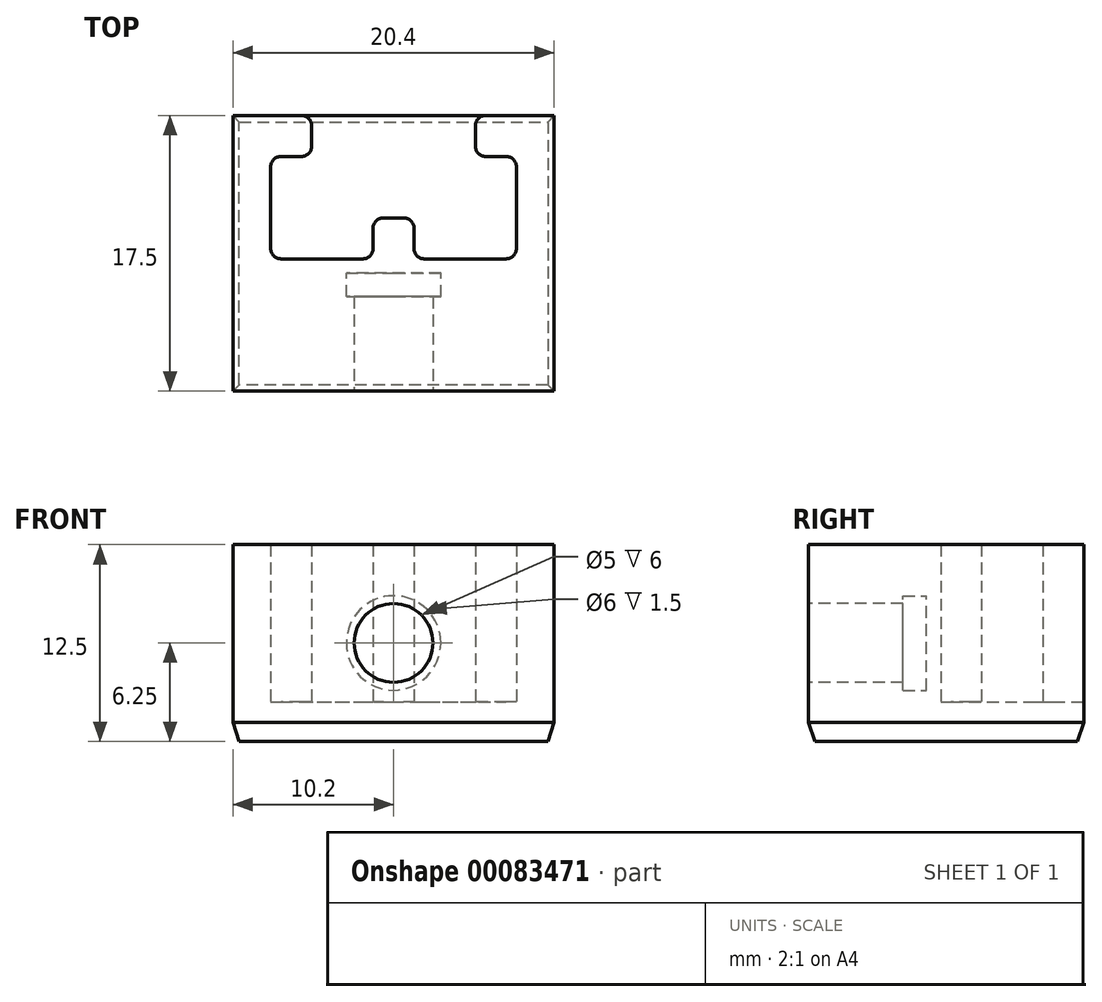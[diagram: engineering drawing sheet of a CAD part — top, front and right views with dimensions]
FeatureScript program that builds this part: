
annotation { "Feature Type Name" : "Feature", "Feature Type Description" : "" }
export const myFeature = defineFeature(function(context is Context, id is Id, definition is map)
    precondition{}
    {
        {
            var Q0;
            Q0=qCreatedBy(makeId("Top.planeOp"),FACE);
            var sketch = newSketch(context, id + "F0", { "sketchPlane" : qUnion([Q0])});
            skLineSegment(sketch, "E0", {"start": v(0, 0) * mm, "end": v(0, 11.5) * mm});
            skLineSegment(sketch, "E1", {"start": v(0, 11.5) * mm, "end": v(5, 11.5) * mm});
            skLineSegment(sketch, "E2", {"start": v(5, 11.5) * mm, "end": v(5, 8.9) * mm});
            skLineSegment(sketch, "E3", {"start": v(5, 8.9) * mm, "end": v(2.4, 8.9) * mm});
            skLineSegment(sketch, "E4", {"start": v(2.4, 8.9) * mm, "end": v(2.4, 2.4) * mm});
            skLineSegment(sketch, "E5", {"start": v(2.4, 2.4) * mm, "end": v(8.9, 2.4) * mm});
            skLineSegment(sketch, "E6", {"start": v(8.9, 2.4) * mm, "end": v(8.9, 5) * mm});
            skLineSegment(sketch, "E7", {"start": v(8.9, 5) * mm, "end": v(11.5, 5) * mm});
            skLineSegment(sketch, "E8", {"start": v(11.5, 5) * mm, "end": v(11.5, 2.4) * mm});
            skLineSegment(sketch, "E9", {"start": v(11.5, 2.4) * mm, "end": v(18, 2.4) * mm});
            skLineSegment(sketch, "E10", {"start": v(18, 2.4) * mm, "end": v(18, 8.9) * mm});
            skLineSegment(sketch, "E11", {"start": v(18, 8.9) * mm, "end": v(15.4, 8.9) * mm});
            skLineSegment(sketch, "E12", {"start": v(15.4, 8.9) * mm, "end": v(15.4, 11.5) * mm});
            skLineSegment(sketch, "E13", {"start": v(15.4, 11.5) * mm, "end": v(20.4, 11.5) * mm});
            skLineSegment(sketch, "E14", {"start": v(20.4, 11.5) * mm, "end": v(20.4, 0) * mm});
            skLineSegment(sketch, "E15", {"start": v(20.4, 0) * mm, "end": v(0, 0) * mm});
            skLineSegment(sketch, "E16", {"start": v(2.4, 2.4) * mm, "end": v(0, 2.4) * mm, "construction": true});
            skLineSegment(sketch, "E17", {"start": v(2.4, 2.4) * mm, "end": v(2.4, 0) * mm, "construction": true});
            skSolve(sketch);
        }
        {
            var Q0;
            Q0=makeQuery(id+"F0.imprint","IMPRINT",FACE,{"disambiguationData":[TD([[makeQuery(id+"F0.imprint","IMPRINT",EDGE,{"derivedFrom":sQuery(id+"F0.wireOp",EDGE,"E0")}),-1.0]])]});
            extrude(context, id + "F1", {"entities" : qUnion([Q0]), "depth" : 10 * mm, "offsetDistance" : 25 * mm});
        }
        {
            var Q0;
            Q0=makeQuery(id+"F1.opExtrude","SWEPT_EDGE",EDGE,{"disambiguationData":[OSD([sQuery(id+"F0.wireOp",EDGE,"E3"),sQuery(id+"F0.wireOp",EDGE,"E4")])]});
            var Q1;
            Q1=makeQuery(id+"F1.opExtrude","SWEPT_EDGE",EDGE,{"disambiguationData":[OSD([sQuery(id+"F0.wireOp",EDGE,"E4"),sQuery(id+"F0.wireOp",EDGE,"E5")])]});
            var Q2;
            Q2=makeQuery(id+"F1.opExtrude","SWEPT_EDGE",EDGE,{"disambiguationData":[OSD([sQuery(id+"F0.wireOp",EDGE,"E8"),sQuery(id+"F0.wireOp",EDGE,"E9")])]});
            var Q3;
            Q3=makeQuery(id+"F1.opExtrude","SWEPT_EDGE",EDGE,{"disambiguationData":[OSD([sQuery(id+"F0.wireOp",EDGE,"E5"),sQuery(id+"F0.wireOp",EDGE,"E6")])]});
            var Q4;
            Q4=makeQuery(id+"F1.opExtrude","SWEPT_EDGE",EDGE,{"disambiguationData":[OSD([sQuery(id+"F0.wireOp",EDGE,"E9"),sQuery(id+"F0.wireOp",EDGE,"E10")])]});
            var Q5;
            Q5=makeQuery(id+"F1.opExtrude","SWEPT_EDGE",EDGE,{"disambiguationData":[OSD([sQuery(id+"F0.wireOp",EDGE,"E10"),sQuery(id+"F0.wireOp",EDGE,"E11")])]});
            var Q6;
            Q6=makeQuery(id+"F1.opExtrude","SWEPT_EDGE",EDGE,{"disambiguationData":[OSD([sQuery(id+"F0.wireOp",EDGE,"E11"),sQuery(id+"F0.wireOp",EDGE,"E12")])]});
            var Q7;
            Q7=makeQuery(id+"F1.opExtrude","SWEPT_EDGE",EDGE,{"disambiguationData":[OSD([sQuery(id+"F0.wireOp",EDGE,"E12"),sQuery(id+"F0.wireOp",EDGE,"E13")])]});
            var Q8;
            Q8=makeQuery(id+"F1.opExtrude","SWEPT_EDGE",EDGE,{"disambiguationData":[OSD([sQuery(id+"F0.wireOp",EDGE,"E2"),sQuery(id+"F0.wireOp",EDGE,"E3")])]});
            var Q9;
            Q9=makeQuery(id+"F1.opExtrude","SWEPT_EDGE",EDGE,{"disambiguationData":[OSD([sQuery(id+"F0.wireOp",EDGE,"E1"),sQuery(id+"F0.wireOp",EDGE,"E2")])]});
            var Q10;
            Q10=makeQuery(id+"F1.opExtrude","SWEPT_EDGE",EDGE,{"disambiguationData":[OSD([sQuery(id+"F0.wireOp",EDGE,"E7"),sQuery(id+"F0.wireOp",EDGE,"E8")])]});
            var Q11;
            Q11=makeQuery(id+"F1.opExtrude","SWEPT_EDGE",EDGE,{"disambiguationData":[OSD([sQuery(id+"F0.wireOp",EDGE,"E6"),sQuery(id+"F0.wireOp",EDGE,"E7")])]});
            fillet(context, id + "F2", {"entities" : qUnion([Q0, Q1, Q2, Q3, Q4, Q5, Q6, Q7, Q8, Q9, Q10, Q11]), "radius" : .65 * mm, "tangentPropagation" : true, "allowEdgeOverflow" : false});
        }
        {
            var Q0;
            Q0=makeQuery(id+"F1.opExtrude","CAP_FACE",FACE,{"disambiguationData":[OSD([sQuery(id+"F0.wireOp",EDGE,"E0"),sQuery(id+"F0.wireOp",EDGE,"E1"),sQuery(id+"F0.wireOp",EDGE,"E2"),sQuery(id+"F0.wireOp",EDGE,"E3"),sQuery(id+"F0.wireOp",EDGE,"E4"),sQuery(id+"F0.wireOp",EDGE,"E5"),sQuery(id+"F0.wireOp",EDGE,"E6"),sQuery(id+"F0.wireOp",EDGE,"E7"),sQuery(id+"F0.wireOp",EDGE,"E8"),sQuery(id+"F0.wireOp",EDGE,"E9"),sQuery(id+"F0.wireOp",EDGE,"E10"),sQuery(id+"F0.wireOp",EDGE,"E11"),sQuery(id+"F0.wireOp",EDGE,"E12"),sQuery(id+"F0.wireOp",EDGE,"E13"),sQuery(id+"F0.wireOp",EDGE,"E14"),sQuery(id+"F0.wireOp",EDGE,"E15")])],"isStart":true});
            var sketch = newSketch(context, id + "F3", { "sketchPlane" : qUnion([Q0])});
            skLineSegment(sketch, "E18.bottom", {"start": v(0, 0) * mm, "end": v(20.4, 0) * mm});
            skLineSegment(sketch, "E18.top", {"start": v(0, -11.5) * mm, "end": v(20.4, -11.5) * mm});
            skLineSegment(sketch, "E18.left", {"start": v(0, 0) * mm, "end": v(0, -11.5) * mm});
            skLineSegment(sketch, "E18.right", {"start": v(20.4, 0) * mm, "end": v(20.4, -11.5) * mm});
            skSolve(sketch);
        }
        {
            var Q0;
            {var subQ7=sQuery(id+"F0.wireOp",EDGE,"E2");Q0=makeQuery(id+"F3.imprint","IMPRINT",FACE,{"disambiguationData":[TD([[makeQuery(id+"F3.imprint","IMPRINT",EDGE,{"derivedFrom":makeQuery(id+"F1.opExtrude","CAP_EDGE",EDGE,{"disambiguationData":[OSD([subQ7])],"isStart":true})}),-1.0]])]});}
            var Q1;
            Q1=makeQuery(id+"F3.imprint","IMPRINT",FACE,{"disambiguationData":[TD([[makeQuery(id+"F3.imprint","IMPRINT",EDGE,{"derivedFrom":sQuery(id+"F3.wireOp",EDGE,"E18.bottom")}),1.0]])]});
            extrude(context, id + "F4", {"entities" : qUnion([Q0, Q1]), "operationType" : NewBodyOperationType.ADD, "depth" : 2.5 * mm, "offsetDistance" : 25 * mm});
        }
        {
            var Q0;
            Q0=qCreatedBy(makeId("Top.planeOp"),FACE);
            var sketch = newSketch(context, id + "F5", { "sketchPlane" : qUnion([Q0])});
            skPoint(sketch, "E19.0", {"position": v(20.4, 0) * mm});
            skLineSegment(sketch, "E20.bottom", {"start": v(0, 0) * mm, "end": v(20.4, 0) * mm});
            skLineSegment(sketch, "E20.top", {"start": v(0, -6) * mm, "end": v(20.4, -6) * mm});
            skLineSegment(sketch, "E20.left", {"start": v(0, 0) * mm, "end": v(0, -6) * mm});
            skLineSegment(sketch, "E20.right", {"start": v(20.4, 0) * mm, "end": v(20.4, -6) * mm});
            skSolve(sketch);
        }
        {
            var Q0;
            Q0=makeQuery(id+"F5.imprint","IMPRINT",FACE,{"disambiguationData":[TD([[makeQuery(id+"F5.imprint","IMPRINT",EDGE,{"derivedFrom":sQuery(id+"F5.wireOp",EDGE,"E20.bottom")}),-1.0]])]});
            var Q1;
            Q1=makeQuery(id+"F1.opExtrude","CAP_FACE",FACE,{"disambiguationData":[OSD([sQuery(id+"F0.wireOp",EDGE,"E0"),sQuery(id+"F0.wireOp",EDGE,"E1"),sQuery(id+"F0.wireOp",EDGE,"E2"),sQuery(id+"F0.wireOp",EDGE,"E3"),sQuery(id+"F0.wireOp",EDGE,"E4"),sQuery(id+"F0.wireOp",EDGE,"E5"),sQuery(id+"F0.wireOp",EDGE,"E6"),sQuery(id+"F0.wireOp",EDGE,"E7"),sQuery(id+"F0.wireOp",EDGE,"E8"),sQuery(id+"F0.wireOp",EDGE,"E9"),sQuery(id+"F0.wireOp",EDGE,"E10"),sQuery(id+"F0.wireOp",EDGE,"E11"),sQuery(id+"F0.wireOp",EDGE,"E12"),sQuery(id+"F0.wireOp",EDGE,"E13"),sQuery(id+"F0.wireOp",EDGE,"E14"),sQuery(id+"F0.wireOp",EDGE,"E15")])],"isStart":false});
            extrude(context, id + "F6", {"entities" : qUnion([Q0]), "operationType" : NewBodyOperationType.ADD, "endBound" : BoundingType.UP_TO_SURFACE, "depth" : 10.3 * mm, "endBoundEntityFace" : qUnion([Q1]), "offsetDistance" : 25 * mm});
        }
        {
            var Q0;
            Q0=makeQuery(id+"F6.opExtrude","CAP_FACE",FACE,{"disambiguationData":[OSD([sQuery(id+"F5.wireOp",EDGE,"E20.bottom"),sQuery(id+"F5.wireOp",EDGE,"E20.top"),sQuery(id+"F5.wireOp",EDGE,"E20.left"),sQuery(id+"F5.wireOp",EDGE,"E20.right")])],"isStart":true});
            var Q1;
            Q1=makeQuery(id+"F4.opExtrude","CAP_FACE",FACE,{"disambiguationData":[OSD([sQuery(id+"F3.wireOp",EDGE,"E18.bottom"),sQuery(id+"F3.wireOp",EDGE,"E18.top"),sQuery(id+"F3.wireOp",EDGE,"E18.left"),sQuery(id+"F3.wireOp",EDGE,"E18.right")])],"isStart":false});
            extrude(context, id + "F7", {"entities" : qUnion([Q0]), "operationType" : NewBodyOperationType.ADD, "endBound" : BoundingType.UP_TO_SURFACE, "depth" : 25 * mm, "endBoundEntityFace" : qUnion([Q1]), "offsetDistance" : 25 * mm});
        }
        {
            var Q0;
            {var subQ0=sQuery(id+"F5.wireOp",EDGE,"E20.top");Q0=makeQuery(id+"F7.boolean.opBoolean","MERGE",FACE,{"derivedFrom":[makeQuery(id+"F6.opExtrude","SWEPT_FACE",FACE,{"disambiguationData":[OSD([subQ0])]}),makeQuery(id+"F7.opExtrude","SWEPT_FACE",FACE,{"disambiguationData":[OSD([subQ0])]})]});}
            var sketch = newSketch(context, id + "F8", { "sketchPlane" : qUnion([Q0])});
            skCircle(sketch, "E21", {"center": v(10.2, 3.75) * mm, "radius": 2.5 * mm});
            skLineSegment(sketch, "E22", {"start": v(10.2, 10) * mm, "end": v(10.2, -2.5) * mm, "construction": true});
            skSolve(sketch);
        }
        {
            var Q0;
            Q0=makeQuery(id+"F8.imprint","IMPRINT",FACE,{"disambiguationData":[TD([[makeQuery(id+"F8.imprint","IMPRINT",EDGE,{"derivedFrom":sQuery(id+"F8.wireOp",EDGE,"E21")}),1.0]])]});
            extrude(context, id + "F9", {"entities" : qUnion([Q0]), "operationType" : NewBodyOperationType.REMOVE, "oppositeDirection" : true, "depth" : 7.5 * mm, "offsetDistance" : 25 * mm});
        }
        {
            var Q0;
            Q0=makeQuery(id+"F9.boolean.opBoolean","COPY",FACE,{"derivedFrom":makeQuery(id+"F9.opExtrude","CAP_FACE",FACE,{"disambiguationData":[OSD([sQuery(id+"F8.wireOp",EDGE,"E21")])],"isStart":false})});
            var sketch = newSketch(context, id + "F10", { "sketchPlane" : qUnion([Q0])});
            skCircle(sketch, "E23.0", {"center": v(10.2, 3.75) * mm, "radius": 2.5 * mm, "construction": true});
            skCircle(sketch, "E24", {"center": v(10.2, 3.75) * mm, "radius": 3 * mm});
            skSolve(sketch);
        }
        {
            var Q0;
            Q0=makeQuery(id+"F10.imprint","IMPRINT",FACE,{"disambiguationData":[TD([[makeQuery(id+"F10.imprint","IMPRINT",EDGE,{"derivedFrom":sQuery(id+"F10.wireOp",EDGE,"E24")}),1.0]])]});
            extrude(context, id + "F11", {"entities" : qUnion([Q0]), "operationType" : NewBodyOperationType.REMOVE, "depth" : 1.5 * mm, "offsetDistance" : 25 * mm});
        }
        {
            var Q0;
            {var subQ0=sQuery(id+"F3.wireOp",EDGE,"E18.right");var subQ1=sQuery(id+"F3.wireOp",EDGE,"E18.left");var subQ2=sQuery(id+"F3.wireOp",EDGE,"E18.top");var subQ3=sQuery(id+"F3.wireOp",EDGE,"E18.bottom");Q0=makeQuery(id+"F7.boolean.opBoolean","MERGE",FACE,{"derivedFrom":[makeQuery(id+"F4.opExtrude","CAP_FACE",FACE,{"disambiguationData":[OSD([subQ3,subQ2,subQ1,subQ0])],"isStart":false}),makeQuery(id+"F7.opExtrude","CAP_FACE",FACE,{"disambiguationData":[OSD([subQ3,subQ2,subQ1,subQ0])],"isStart":false})]});}
            chamfer(context, id + "F12", {"entities" : qUnion([Q0]), "chamferType" : ChamferType.TWO_OFFSETS, "width1" : .4 * mm, "oppositeDirection" : false, "width2" : 1.2 * mm, "tangentPropagation" : true});
        }
    });
